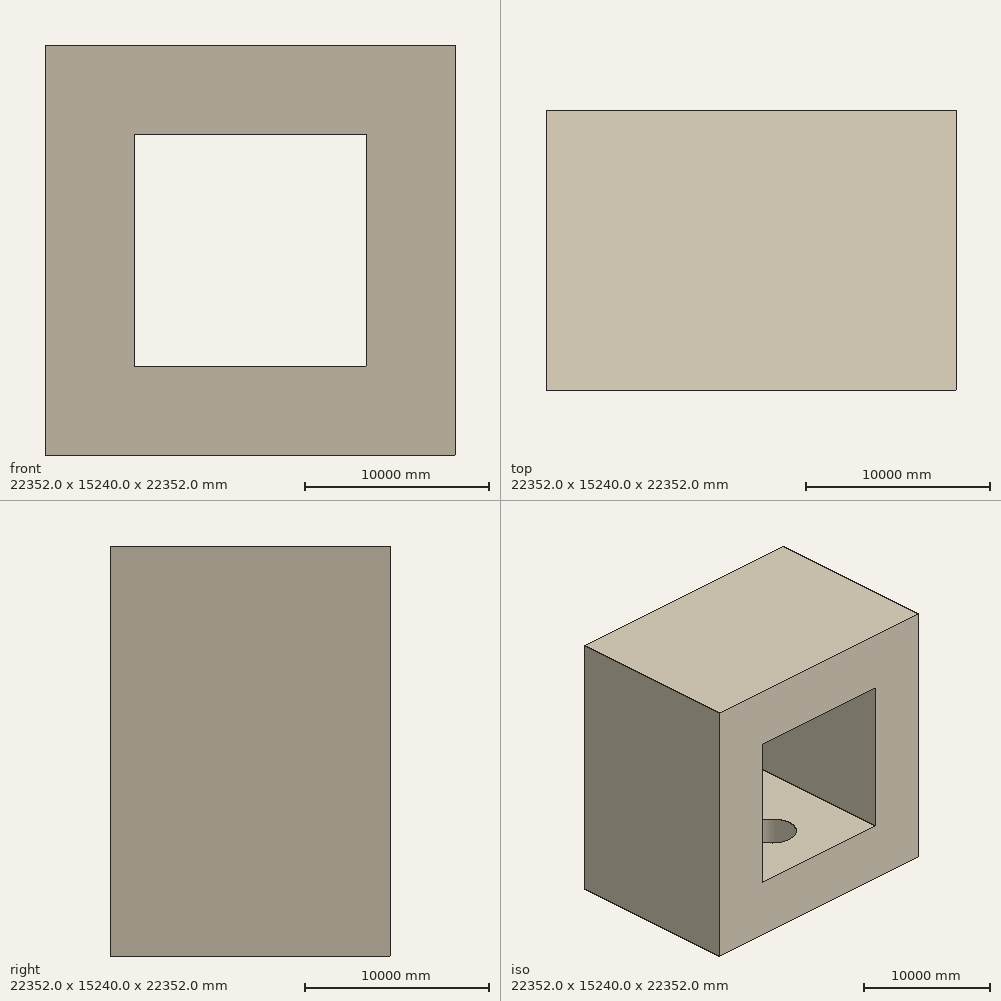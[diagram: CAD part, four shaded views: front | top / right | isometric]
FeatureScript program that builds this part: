
annotation { "Feature Type Name" : "Feature", "Feature Type Description" : "" }
export const myFeature = defineFeature(function(context is Context, id is Id, definition is map)
    precondition{}
    {
        {
            var Q0;
            Q0=qCreatedBy(makeId("Front.planeOp"),FACE);
            var sketch = newSketch(context, id + "F0", { "sketchPlane" : qUnion([Q0])});
            skLineSegment(sketch, "E0.bottom", {"start": v(6350, 6350) * mm, "end": v(-6350, 6350) * mm});
            skLineSegment(sketch, "E0.top", {"start": v(6350, -6350) * mm, "end": v(-6350, -6350) * mm});
            skLineSegment(sketch, "E0.left", {"start": v(6350, 6350) * mm, "end": v(6350, -6350) * mm});
            skLineSegment(sketch, "E0.right", {"start": v(-6350, 6350) * mm, "end": v(-6350, -6350) * mm});
            skPoint(sketch, "E0.middle", {"position": v(0, 0) * mm});
            skLineSegment(sketch, "E1.bottom", {"start": v(-11176, 11176) * mm, "end": v(11176, 11176) * mm});
            skLineSegment(sketch, "E1.top", {"start": v(-11176, -11176) * mm, "end": v(11176, -11176) * mm});
            skLineSegment(sketch, "E1.left", {"start": v(-11176, 11176) * mm, "end": v(-11176, -11176) * mm});
            skLineSegment(sketch, "E1.right", {"start": v(11176, 11176) * mm, "end": v(11176, -11176) * mm});
            skSolve(sketch);
        }
        {
            var Q0;
            Q0 = qSketchRegion(id + "F0", true);
            extrude(context, id + "F1", {"entities" : qUnion([Q0]), "depth" : 15240 * mm, "offsetDistance" : 25.4 * mm});
        }
        {
            var Q0;
            Q0=makeQuery(id+"F1.opExtrude","SWEPT_FACE",FACE,{"disambiguationData":[OSD([sQuery(id+"F0.wireOp",EDGE,"E1.top")])]});
            var sketch = newSketch(context, id + "F2", { "sketchPlane" : qUnion([Q0])});
            skCircle(sketch, "E2", {"center": v(0, 9983.42) * mm, "radius": 1905 * mm});
            skLineSegment(sketch, "E3", {"start": v(0, 15240) * mm, "end": v(0, 0) * mm});
            skSolve(sketch);
        }
        {
            var Q0;
            Q0 = qSketchRegion(id + "F2", true);
            extrude(context, id + "F3", {"entities" : qUnion([Q0]), "operationType" : NewBodyOperationType.REMOVE, "endBound" : BoundingType.UP_TO_NEXT, "oppositeDirection" : true, "depth" : 25 * mm, "offsetDistance" : 25 * mm});
        }
    });
